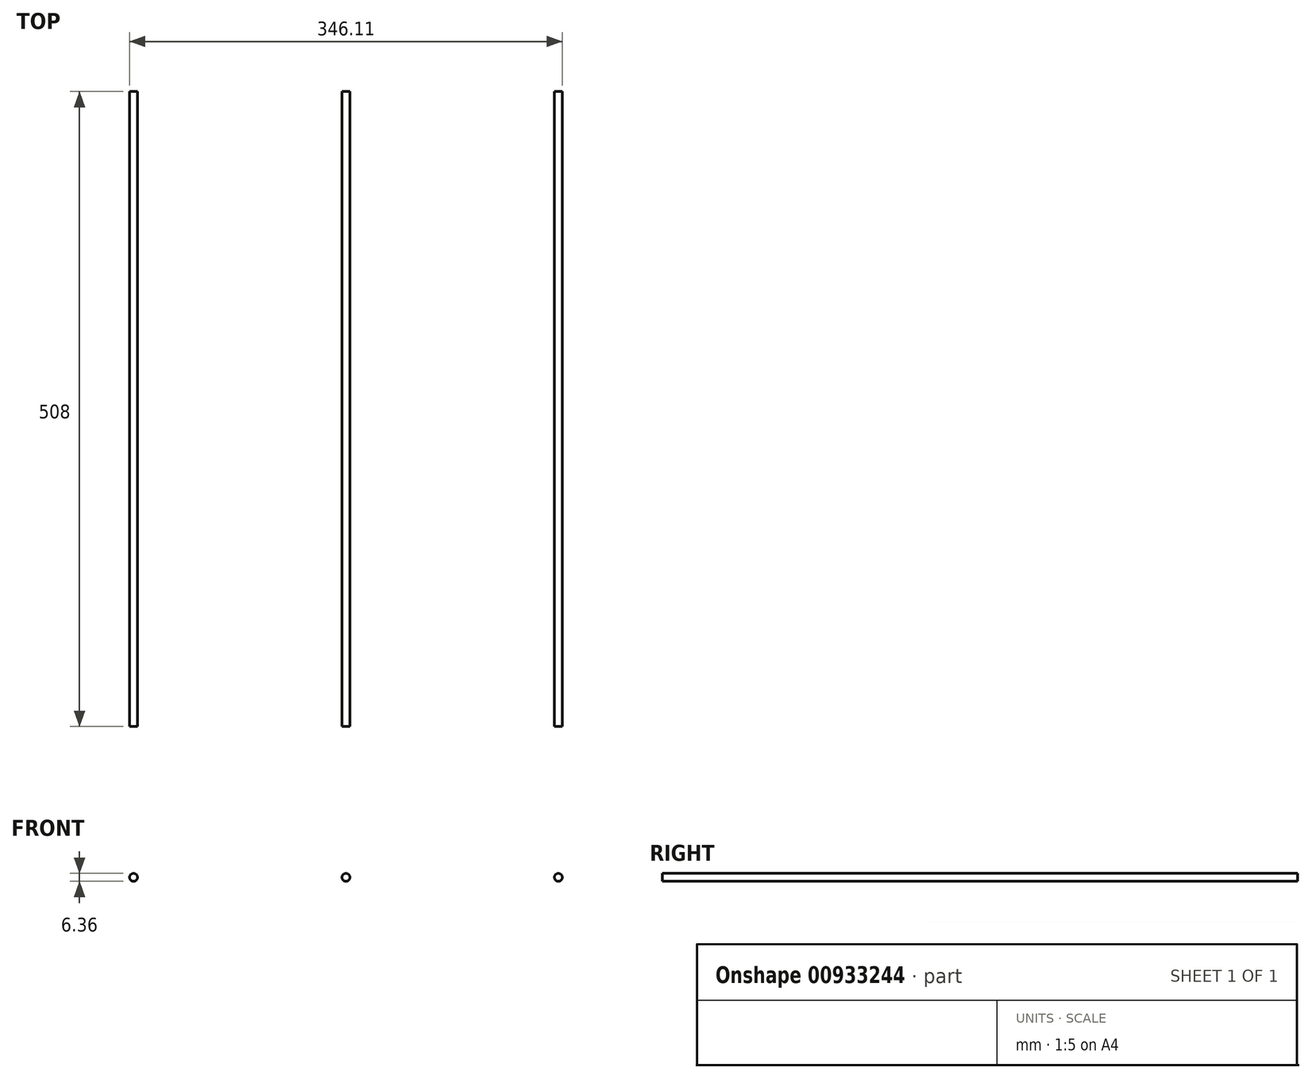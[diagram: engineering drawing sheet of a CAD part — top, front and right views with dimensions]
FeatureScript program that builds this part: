
annotation { "Feature Type Name" : "Feature", "Feature Type Description" : "" }
export const myFeature = defineFeature(function(context is Context, id is Id, definition is map)
    precondition{}
    {
        {
            var Q0;
            Q0=qCreatedBy(makeId("Front.planeOp"),FACE);
            var sketch = newSketch(context, id + "F0", { "sketchPlane" : qUnion([Q0])});
            skCircle(sketch, "E0", {"center": v(0, 0) * mm, "radius": 3.18 * mm});
            skCircle(sketch, "E1.1.0.0", {"center": v(169.88, 0) * mm, "radius": 3.18 * mm});
            skCircle(sketch, "E1.2.0.0", {"center": v(339.75, 0) * mm, "radius": 3.18 * mm});
            skSolve(sketch);
        }
        {
            var Q0;
            Q0=sQuery(id+"F0.wireOp",EDGE,"E0");
            var Q1;
            Q1=sQuery(id+"F0.wireOp",EDGE,"E1.1.0.0");
            var Q2;
            Q2=sQuery(id+"F0.wireOp",EDGE,"E1.2.0.0");
            extrude(context, id + "F1", {"bodyType" : ToolBodyType.SURFACE, "surfaceEntities" : qUnion([Q0, Q1, Q2]), "depth" : 508 * mm, "offsetDistance" : 25.4 * mm});
        }
    });
